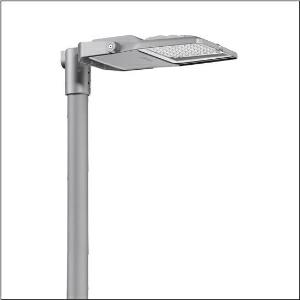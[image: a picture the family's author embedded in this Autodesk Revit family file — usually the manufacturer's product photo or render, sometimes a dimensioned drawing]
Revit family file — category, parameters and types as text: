
# Revit family: floodlight_fl_21_mini___pl64_5xa7776c2e3a_3ffb
name_source: partatom
category: Lighting Fixtures
units: mm (PartAtom-declared; Revit-internal decimal feet)

## family parameters
Cut with Voids When Loaded = No
Host = Face
Light Source = No
Part Type = Normal
Room Calculation Point = No
Round Connector Dimension = Use Diameter
Shared = No

## types (1)
- --- (1 x LED, 11770 lm, 89 W, 3000K)
    Apparent Load = 89 VA
    CIE Flux Codes = 28 80 98 100 100
    Color Rendering = 70
    Color Temperature = 3000K
    Default Elevation = 1800 mm
    Description = Floodlight FL 21 mini, floodlight, primary light control with lens, of PMMA, primary optical cover: protective disc, of toughened safety glass, transparent, light distribution: PL64, light emission: direct distribution, installation type: surface-mounted, LED, High Power LED, rated luminous flux: 11.770lm, luminous efficacy: 132lm/W, light colour: 730, colour temperature: 3000K, control: flexible luminous flux parameterisation, time-dependent luminous flux control, constant luminous flux control, overheat protection, presetting dimming logarithmic, with terminal, 6-pole, mains connection: 220..240V, AC, 50/60Hz, start of lifetime: 89W, end of service life: 94W, reduction: 43W, luminaire housing, of diecast aluminium, powder-coated, Siteco® metallic grey (DB 702S), corrosivity category C5 mid according to DIN EN ISO 12944, sealing non-destructively replaceable, please order mast flange separately, mast bracket, of steel, galvanised, powder-coated, Siteco® metallic grey (DB 702S), Smart Interface below and above, protection rating (complete): IP66, insulation class (complete): insulation class II (safety insulation), certification: CE, ENEC, VDE, protection symbol: D, impact resistance: IK08, permissible operating ambient temperature: -40..+40°C, permissible operating ambient temperature for outdoor applications: -40..+50°C, standard: DIN EN 12944, LABS conformity tested according to VDMA 24364:2018-05, packaging unit: 1 piece

Light Distribution: PL64
    Height = 70 mm
    Lamp = 1 x LED
    Lamp Light Flux = 11770 lm
    Lamp Power = 89 W
    Lamp count = 1
    Length = 485 mm
    Luminous efficacy = 132 lm/W
    Manufacturer = Siteco
    ModVariant = No
    Model = 5XA7776C2E3A
    Number of Poles = 1
    OnlyDefault = Yes
    Power Factor = 1
    Product Name = Floodlight FL 21 mini | PL64
    Product group = floodlight | pylon annexe
    ProductGroupID = 6200
    Protection Class = Protection class II
    Protection Degree = IP 66
    RLX_Detail_Level = 1
    RLX_Emergency_Light_Flux = 0 lm
    RLX_Emergency_Type = 0
    RLX_Emergency_Type_DB = No
    RlxData = <blob elided: 100817 chars, md5=240d1568>
    Socket = socket
    Standby Power = 0 W
    System Light Flux = 11770 lm
    System Power = 89 W
    Type Comments = factory setting: luminous flux: 100 % | dim-lin: 254 | 456 mA
    Type Image = l_1007125.jpg
    URL = http://relux.com
    VarID = @adj_097647
    Voltage = 0 V
    Weight = 0.00 kg
    Width = 337 mm

## geometry (parser evidence)
native form markers: Blend x4, Sweep x13
no freeform markers — native parametric forms only
